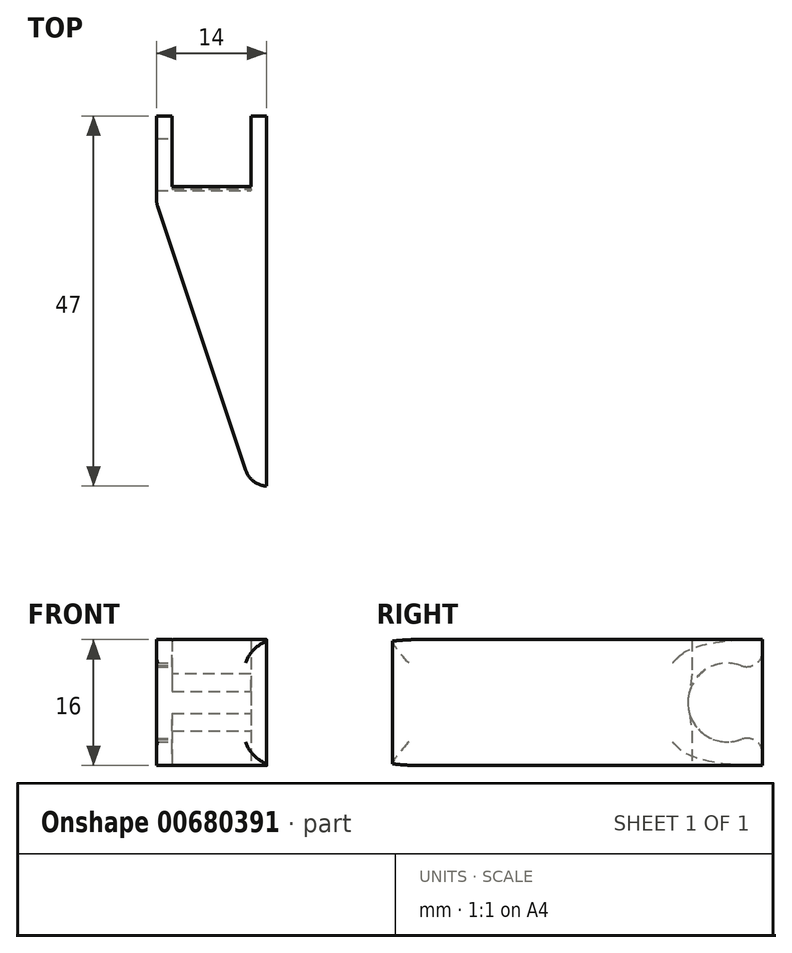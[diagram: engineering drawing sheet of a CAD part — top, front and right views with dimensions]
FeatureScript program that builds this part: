
annotation { "Feature Type Name" : "Feature", "Feature Type Description" : "" }
export const myFeature = defineFeature(function(context is Context, id is Id, definition is map)
    precondition{}
    {
        {
            var Q0;
            Q0=qCreatedBy(makeId("Top.planeOp"),FACE);
            var sketch = newSketch(context, id + "F0", { "sketchPlane" : qUnion([Q0])});
            skLineSegment(sketch, "E0", {"start": v(0, 23.67) * mm, "end": v(0, -23.33) * mm});
            skLineSegment(sketch, "E1", {"start": v(0, -23.33) * mm, "end": v(-2, -23.33) * mm});
            skLineSegment(sketch, "E2", {"start": v(-14, 12.67) * mm, "end": v(-14, 23.67) * mm});
            skLineSegment(sketch, "E3", {"start": v(-14, 23.67) * mm, "end": v(-12, 23.67) * mm});
            skLineSegment(sketch, "E4", {"start": v(-12, 23.67) * mm, "end": v(-12, 14.7) * mm});
            skLineSegment(sketch, "E5", {"start": v(-12, 14.7) * mm, "end": v(-2, 14.7) * mm});
            skLineSegment(sketch, "E6", {"start": v(-2, 14.7) * mm, "end": v(-2, 23.67) * mm});
            skLineSegment(sketch, "E7", {"start": v(-2, 23.67) * mm, "end": v(0, 23.67) * mm});
            skLineSegment(sketch, "E8", {"start": v(-14, 12.67) * mm, "end": v(-2, -23.33) * mm});
            skSolve(sketch);
        }
        {
            var Q0;
            Q0 = qSketchRegion(id + "F0", true);
            extrude(context, id + "F1", {"entities" : qUnion([Q0]), "depth" : 16 * mm, "offsetDistance" : 25 * mm});
        }
        {
            var Q0;
            Q0=makeQuery(id+"F1.opExtrude","SWEPT_FACE",FACE,{"disambiguationData":[OSD([sQuery(id+"F0.wireOp",EDGE,"E4")])]});
            var sketch = newSketch(context, id + "F2", { "sketchPlane" : qUnion([Q0])});
            skCircle(sketch, "E9", {"center": v(19.18, 8) * mm, "radius": 5 * mm});
            skPoint(sketch, "E9.centerSnap0", {"position": v(23.67, 8) * mm});
            skPoint(sketch, "E9.centerSnap1", {"position": v(19.18, 0) * mm});
            skSolve(sketch);
        }
        {
            var Q0;
            Q0 = qSketchRegion(id + "F2", true);
            extrude(context, id + "F3", {"entities" : qUnion([Q0]), "operationType" : NewBodyOperationType.REMOVE, "oppositeDirection" : true, "depth" : 5 * mm, "offsetDistance" : 25 * mm});
        }
        {
            var Q0;
            Q0=makeQuery(id+"F3.boolean.opBoolean","INTERSECT",EDGE,{"disambiguationData":[OD(1.0)],"derivedFrom":[makeQuery(id+"F1.opExtrude","SWEPT_FACE",FACE,{"disambiguationData":[OSD([sQuery(id+"F0.wireOp",EDGE,"E3")])]}),makeQuery(id+"F3.opExtrude","SWEPT_FACE",FACE,{"disambiguationData":[OSD([sQuery(id+"F2.wireOp",EDGE,"E9")])]})]});
            var Q1;
            Q1=makeQuery(id+"F3.boolean.opBoolean","INTERSECT",EDGE,{"disambiguationData":[OD(0.0)],"derivedFrom":[makeQuery(id+"F1.opExtrude","SWEPT_FACE",FACE,{"disambiguationData":[OSD([sQuery(id+"F0.wireOp",EDGE,"E3")])]}),makeQuery(id+"F3.opExtrude","SWEPT_FACE",FACE,{"disambiguationData":[OSD([sQuery(id+"F2.wireOp",EDGE,"E9")])]})]});
            chamfer(context, id + "F4", {"entities" : qUnion([Q0, Q1]), "chamferType" : ChamferType.TWO_OFFSETS, "width1" : 5 * mm, "oppositeDirection" : false, "width2" : 4 * mm, "tangentPropagation" : true});
        }
        {
            var Q0;
            Q0 = qSketchRegion(id + "F2", true);
            extrude(context, id + "F5", {"entities" : qUnion([Q0]), "operationType" : NewBodyOperationType.REMOVE, "depth" : 10 * mm, "offsetDistance" : 25 * mm});
        }
        {
            var Q0;
            Q0=makeQuery(id+"F5.boolean.opBoolean","INTERSECT",EDGE,{"disambiguationData":[OD(0.0)],"derivedFrom":[makeQuery(id+"F1.opExtrude","SWEPT_FACE",FACE,{"disambiguationData":[OSD([sQuery(id+"F0.wireOp",EDGE,"E5")])]}),makeQuery(id+"F5.opExtrude","SWEPT_FACE",FACE,{"disambiguationData":[OSD([sQuery(id+"F2.wireOp",EDGE,"E9")])]})]});
            var Q1;
            Q1=makeQuery(id+"F5.boolean.opBoolean","INTERSECT",EDGE,{"disambiguationData":[OD(1.0)],"derivedFrom":[makeQuery(id+"F1.opExtrude","SWEPT_FACE",FACE,{"disambiguationData":[OSD([sQuery(id+"F0.wireOp",EDGE,"E5")])]}),makeQuery(id+"F5.opExtrude","SWEPT_FACE",FACE,{"disambiguationData":[OSD([sQuery(id+"F2.wireOp",EDGE,"E9")])]})]});
            chamfer(context, id + "F6", {"entities" : qUnion([Q0, Q1]), "width" : 8 * mm, "tangentPropagation" : true});
        }
        {
            var Q0;
            Q0=makeQuery(id+"F1.opExtrude","SWEPT_FACE",FACE,{"disambiguationData":[OSD([sQuery(id+"F0.wireOp",EDGE,"E8")])]});
            fillet(context, id + "F7", {"entities" : qUnion([Q0]), "radius" : 3 * mm, "tangentPropagation" : true, "allowEdgeOverflow" : false});
        }
        {
            var Q0;
            {var subQ0=sQuery(id+"F0.wireOp",EDGE,"E4");var subQ1=sQuery(id+"F0.wireOp",EDGE,"E3");var subQ2=sQuery(id+"F0.wireOp",EDGE,"E2");var subQ3=makeQuery(id+"F3.opExtrude","SWEPT_FACE",FACE,{"disambiguationData":[OSD([sQuery(id+"F2.wireOp",EDGE,"E9")])]});var subQ4=makeQuery(id+"F1.opExtrude","SWEPT_FACE",FACE,{"disambiguationData":[OSD([subQ1])]});Q0=makeQuery(id+"F4.opChamfer","BLEND_EDGE",EDGE,{"blendedFrom":[makeQuery(id+"F3.boolean.opBoolean","INTERSECT",EDGE,{"disambiguationData":[OD(1.0)],"derivedFrom":[subQ4,subQ3]}),makeQuery(id+"F3.boolean.opBoolean","SPLIT",FACE,{"disambiguationData":[TD([makeQuery(id+"F1.opExtrude","CAP_FACE",FACE,{"disambiguationData":[OSD([sQuery(id+"F0.wireOp",EDGE,"E0"),sQuery(id+"F0.wireOp",EDGE,"E1"),subQ2,subQ1,subQ0,sQuery(id+"F0.wireOp",EDGE,"E5"),sQuery(id+"F0.wireOp",EDGE,"E6"),sQuery(id+"F0.wireOp",EDGE,"E7"),sQuery(id+"F0.wireOp",EDGE,"E8")])],"isStart":false})])],"derivedFrom":subQ4})],"blendedInto":[makeQuery(id+"F3.boolean.opBoolean","SPLIT",FACE,{"disambiguationData":[TD([makeQuery(id+"F1.opExtrude","CAP_FACE",FACE,{"disambiguationData":[OSD([sQuery(id+"F0.wireOp",EDGE,"E0"),sQuery(id+"F0.wireOp",EDGE,"E1"),subQ2,subQ1,subQ0,sQuery(id+"F0.wireOp",EDGE,"E5"),sQuery(id+"F0.wireOp",EDGE,"E6"),sQuery(id+"F0.wireOp",EDGE,"E7"),sQuery(id+"F0.wireOp",EDGE,"E8")])],"isStart":false})])],"derivedFrom":subQ4})]});}
            var Q1;
            {var subQ0=sQuery(id+"F0.wireOp",EDGE,"E4");var subQ1=sQuery(id+"F0.wireOp",EDGE,"E3");var subQ2=sQuery(id+"F0.wireOp",EDGE,"E2");var subQ3=makeQuery(id+"F3.opExtrude","SWEPT_FACE",FACE,{"disambiguationData":[OSD([sQuery(id+"F2.wireOp",EDGE,"E9")])]});var subQ4=makeQuery(id+"F1.opExtrude","SWEPT_FACE",FACE,{"disambiguationData":[OSD([subQ1])]});Q1=makeQuery(id+"F4.opChamfer","BLEND_EDGE",EDGE,{"blendedFrom":[makeQuery(id+"F3.boolean.opBoolean","INTERSECT",EDGE,{"disambiguationData":[OD(0.0)],"derivedFrom":[subQ4,subQ3]}),makeQuery(id+"F3.boolean.opBoolean","SPLIT",FACE,{"disambiguationData":[TD([makeQuery(id+"F1.opExtrude","CAP_FACE",FACE,{"disambiguationData":[OSD([sQuery(id+"F0.wireOp",EDGE,"E0"),sQuery(id+"F0.wireOp",EDGE,"E1"),subQ2,subQ1,subQ0,sQuery(id+"F0.wireOp",EDGE,"E5"),sQuery(id+"F0.wireOp",EDGE,"E6"),sQuery(id+"F0.wireOp",EDGE,"E7"),sQuery(id+"F0.wireOp",EDGE,"E8")])],"isStart":true})])],"derivedFrom":subQ4})],"blendedInto":[makeQuery(id+"F3.boolean.opBoolean","SPLIT",FACE,{"disambiguationData":[TD([makeQuery(id+"F1.opExtrude","CAP_FACE",FACE,{"disambiguationData":[OSD([sQuery(id+"F0.wireOp",EDGE,"E0"),sQuery(id+"F0.wireOp",EDGE,"E1"),subQ2,subQ1,subQ0,sQuery(id+"F0.wireOp",EDGE,"E5"),sQuery(id+"F0.wireOp",EDGE,"E6"),sQuery(id+"F0.wireOp",EDGE,"E7"),sQuery(id+"F0.wireOp",EDGE,"E8")])],"isStart":true})])],"derivedFrom":subQ4})]});}
            fillet(context, id + "F8", {"entities" : qUnion([Q0, Q1]), "radius" : 2 * mm, "tangentPropagation" : true, "allowEdgeOverflow" : false});
        }
    });
